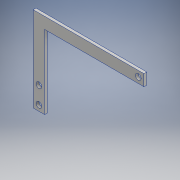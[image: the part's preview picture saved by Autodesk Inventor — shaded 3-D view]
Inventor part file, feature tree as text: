
AUTODESK INVENTOR PART (.ipt)
format: ipt  version: 2018.1 (Build 221171000, 171)  size: 113,664 bytes
history: native  units: mm
features: extrude x1, sketch x1
ambient origin geometry x8: Origin, YZ Plane, XZ Plane, XY Plane, X Axis, Y Axis, Z Axis, Center Point
bodies: Body1 (feature_tree)
feature tree (2):
  extrude  "押し出し4"  Depth=195.0mm
  sketch  "スケッチ1"
